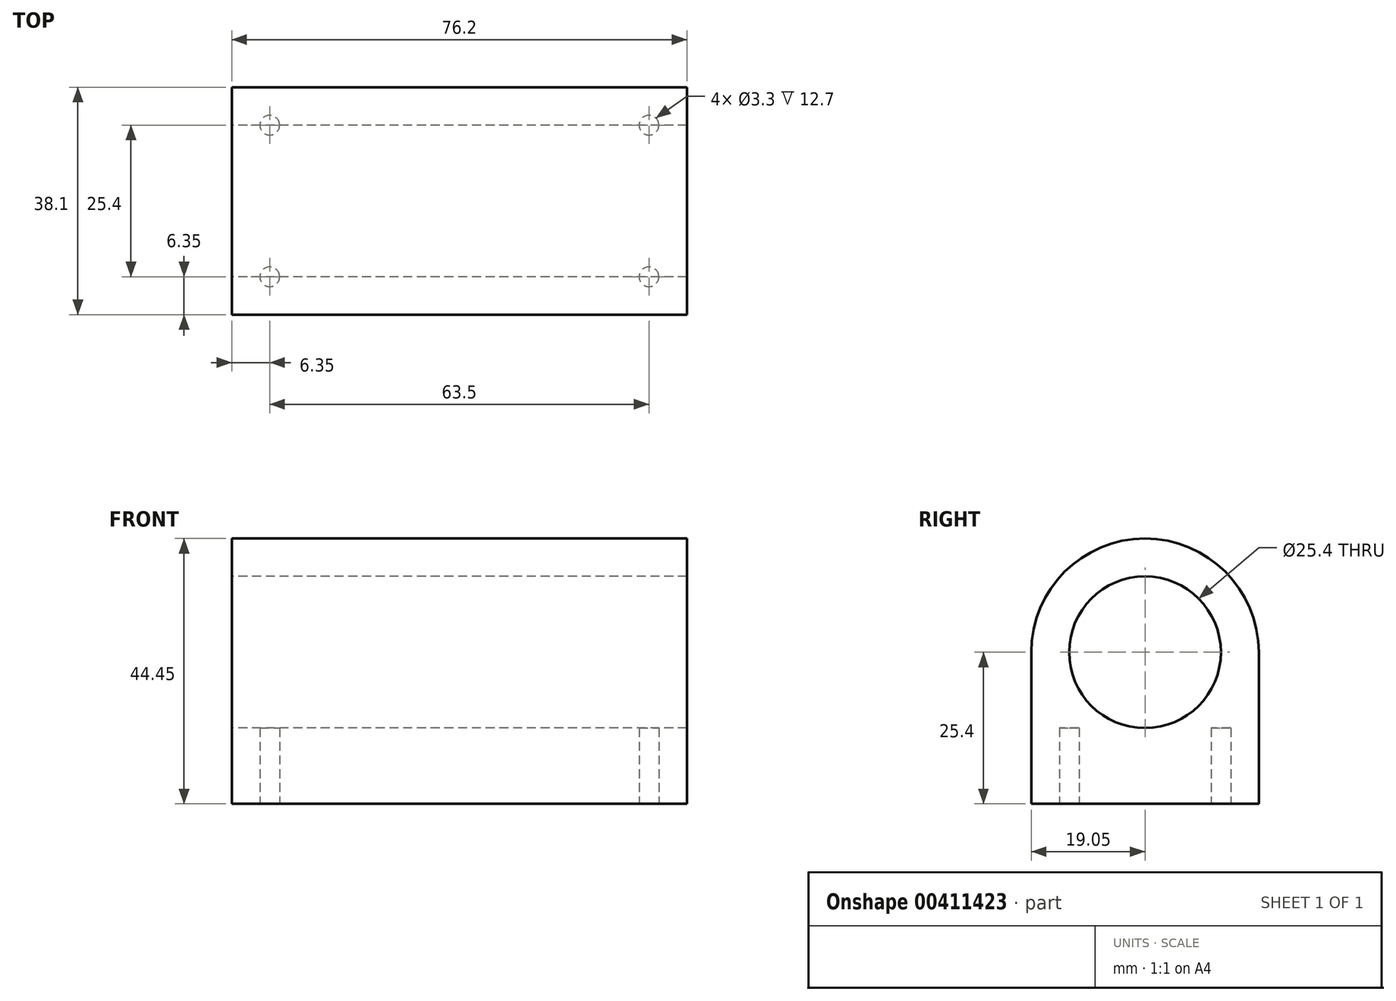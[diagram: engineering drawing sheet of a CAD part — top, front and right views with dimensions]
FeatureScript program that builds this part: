
annotation { "Feature Type Name" : "Feature", "Feature Type Description" : "" }
export const myFeature = defineFeature(function(context is Context, id is Id, definition is map)
    precondition{}
    {
        {
            var Q0;
            Q0=qCreatedBy(makeId("Right.planeOp"),FACE);
            var sketch = newSketch(context, id + "F0", { "sketchPlane" : qUnion([Q0])});
            skArc(sketch, "E0", {"start": v(19.05, 0) * mm, "mid": v(0, 19.05) * mm, "end": v(-19.05, 0) * mm});
            skCircle(sketch, "E1", {"center": v(0, 0) * mm, "radius": 12.7 * mm});
            skLineSegment(sketch, "E2", {"start": v(-19.05, 0) * mm, "end": v(-19.05, -25.4) * mm});
            skLineSegment(sketch, "E3", {"start": v(-19.05, -25.4) * mm, "end": v(0, -25.4) * mm});
            skLineSegment(sketch, "E4.MirrorCS", {"start": v(19.05, -25.4) * mm, "end": v(0, -25.4) * mm});
            skLineSegment(sketch, "E5.MirrorCS", {"start": v(19.05, 0) * mm, "end": v(19.05, -25.4) * mm});
            skSolve(sketch);
        }
        {
            var Q0;
            Q0 = qSketchRegion(id + "F0", true);
            extrude(context, id + "F1", {"entities" : qUnion([Q0]), "endBound" : BoundingType.SYMMETRIC, "depth" : 76.2 * mm});
        }
        {
            var Q0;
            Q0=makeQuery(id+"F1.opExtrude","SWEPT_FACE",FACE,{"disambiguationData":[OSD([sQuery(id+"F0.wireOp",EDGE,"E3"),sQuery(id+"F0.wireOp",EDGE,"E4.MirrorCS")])]});
            var sketch = newSketch(context, id + "F2", { "sketchPlane" : qUnion([Q0])});
            skCircle(sketch, "E6", {"center": v(-31.75, 12.7) * mm, "radius": 1.65 * mm});
            skCircle(sketch, "E7.MirrorC", {"center": v(-31.75, -12.7) * mm, "radius": 1.65 * mm});
            skCircle(sketch, "E8.MirrorC", {"center": v(31.75, 12.7) * mm, "radius": 1.65 * mm});
            skCircle(sketch, "E9.MirrorC", {"center": v(31.75, -12.7) * mm, "radius": 1.65 * mm});
            skSolve(sketch);
        }
        {
            var Q0;
            Q0 = qSketchRegion(id + "F2", true);
            extrude(context, id + "F3", {"entities" : qUnion([Q0]), "operationType" : NewBodyOperationType.REMOVE, "oppositeDirection" : true, "depth" : 12.7 * mm});
        }
    });
